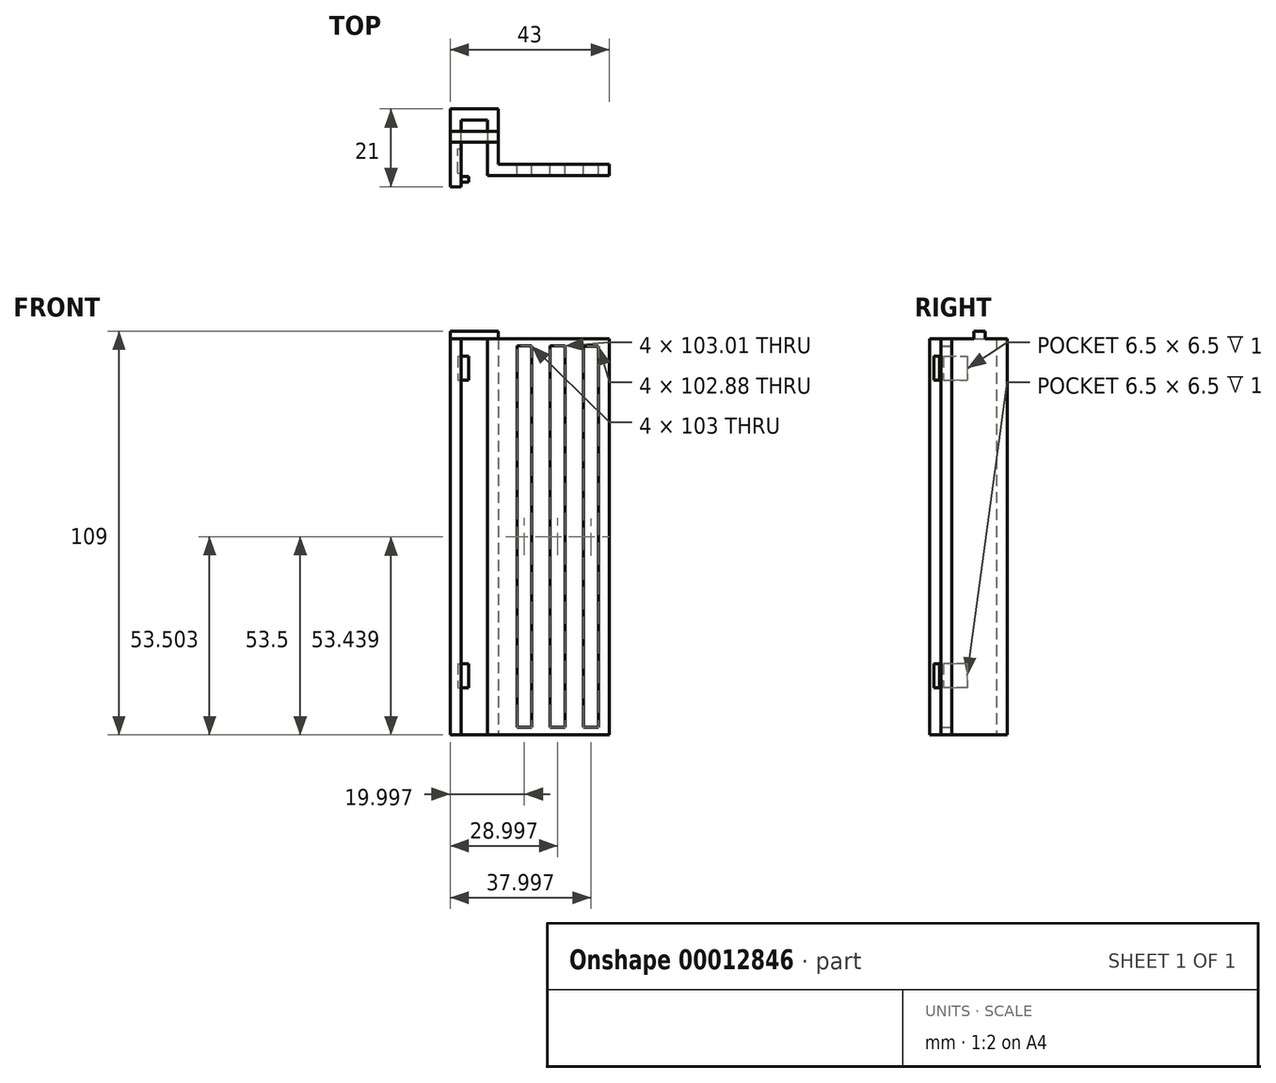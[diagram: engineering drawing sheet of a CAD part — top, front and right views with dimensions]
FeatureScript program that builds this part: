
annotation { "Feature Type Name" : "Feature", "Feature Type Description" : "" }
export const myFeature = defineFeature(function(context is Context, id is Id, definition is map)
    precondition{}
    {
        {
            var Q0;
            Q0=qCreatedBy(makeId("Top.planeOp"),FACE);
            var sketch = newSketch(context, id + "F0", { "sketchPlane" : qUnion([Q0])});
            skLineSegment(sketch, "E0", {"start": v(-54.2, 35.8) * mm, "end": v(-54.2, 56.8) * mm});
            skLineSegment(sketch, "E1", {"start": v(-54.2, 56.8) * mm, "end": v(-41.2, 56.8) * mm});
            skLineSegment(sketch, "E2", {"start": v(-41.2, 56.8) * mm, "end": v(-41.2, 41.8) * mm});
            skLineSegment(sketch, "E3", {"start": v(-41.2, 41.8) * mm, "end": v(-11.2, 41.8) * mm});
            skLineSegment(sketch, "E4", {"start": v(-54.2, 35.8) * mm, "end": v(-51.2, 35.8) * mm});
            skLineSegment(sketch, "E5", {"start": v(-51.2, 35.8) * mm, "end": v(-51.2, 53.8) * mm});
            skLineSegment(sketch, "E6", {"start": v(-51.2, 53.8) * mm, "end": v(-44.2, 53.8) * mm});
            skLineSegment(sketch, "E7", {"start": v(-44.2, 53.8) * mm, "end": v(-44.2, 38.8) * mm});
            skLineSegment(sketch, "E8", {"start": v(-44.2, 38.8) * mm, "end": v(-11.2, 38.8) * mm});
            skLineSegment(sketch, "E9", {"start": v(-11.2, 38.8) * mm, "end": v(-11.2, 41.8) * mm});
            skSolve(sketch);
        }
        {
            var Q0;
            Q0=makeQuery(id+"F0.imprint","IMPRINT",FACE,{"disambiguationData":[TD([[makeQuery(id+"F0.imprint","IMPRINT",EDGE,{"derivedFrom":sQuery(id+"F0.wireOp",EDGE,"E0")}),-1.0]])]});
            extrude(context, id + "F1", {"entities" : qUnion([Q0]), "depth" : 107 * mm});
        }
        {
            var Q0;
            Q0=makeQuery(id+"F1.opExtrude","SWEPT_FACE",FACE,{"disambiguationData":[OSD([sQuery(id+"F0.wireOp",EDGE,"E5")])]});
            var sketch = newSketch(context, id + "F2", { "sketchPlane" : qUnion([Q0])});
            skLineSegment(sketch, "E10.bottom", {"start": v(46, 19.2) * mm, "end": v(39.5, 19.2) * mm});
            skLineSegment(sketch, "E10.top", {"start": v(46, 12.7) * mm, "end": v(39.5, 12.7) * mm});
            skLineSegment(sketch, "E10.left", {"start": v(46, 19.2) * mm, "end": v(46, 12.7) * mm});
            skLineSegment(sketch, "E10.right", {"start": v(39.5, 19.2) * mm, "end": v(39.5, 12.7) * mm});
            skLineSegment(sketch, "E11.bottom", {"start": v(39.5, 102.2) * mm, "end": v(46, 102.2) * mm});
            skLineSegment(sketch, "E11.top", {"start": v(39.5, 95.7) * mm, "end": v(46, 95.7) * mm});
            skLineSegment(sketch, "E11.left", {"start": v(39.5, 102.2) * mm, "end": v(39.5, 95.7) * mm});
            skLineSegment(sketch, "E11.right", {"start": v(46, 102.2) * mm, "end": v(46, 95.7) * mm});
            skSolve(sketch);
        }
        {
            var Q0;
            Q0=qSketchRegion(id+"F2",true);
            extrude(context, id + "F3", {"entities" : qUnion([Q0]), "operationType" : NewBodyOperationType.REMOVE, "oppositeDirection" : true, "depth" : 1 * mm});
        }
        {
            var Q0;
            Q0=makeQuery(id+"F1.opExtrude","SWEPT_FACE",FACE,{"disambiguationData":[OSD([sQuery(id+"F0.wireOp",EDGE,"E5")])]});
            var sketch = newSketch(context, id + "F4", { "sketchPlane" : qUnion([Q0])});
            skLineSegment(sketch, "E12.bottom", {"start": v(38.5, 102.2) * mm, "end": v(37, 102.2) * mm});
            skLineSegment(sketch, "E12.top", {"start": v(38.5, 95.7) * mm, "end": v(37, 95.7) * mm});
            skLineSegment(sketch, "E12.left", {"start": v(38.5, 102.2) * mm, "end": v(38.5, 95.7) * mm});
            skLineSegment(sketch, "E12.right", {"start": v(37, 102.2) * mm, "end": v(37, 95.7) * mm});
            skLineSegment(sketch, "E13.bottom", {"start": v(38.5, 19.2) * mm, "end": v(37, 19.2) * mm});
            skLineSegment(sketch, "E13.top", {"start": v(38.5, 12.7) * mm, "end": v(37, 12.7) * mm});
            skLineSegment(sketch, "E13.left", {"start": v(38.5, 19.2) * mm, "end": v(38.5, 12.7) * mm});
            skLineSegment(sketch, "E13.right", {"start": v(37, 19.2) * mm, "end": v(37, 12.7) * mm});
            skSolve(sketch);
        }
        {
            var Q0;
            Q0 = qSketchRegion(id + "F4", true);
            extrude(context, id + "F5", {"entities" : qUnion([Q0]), "operationType" : NewBodyOperationType.ADD, "depth" : 2 * mm});
        }
        {
            var Q0;
            Q0=makeQuery(id+"F1.opExtrude","SWEPT_FACE",FACE,{"disambiguationData":[OSD([sQuery(id+"F0.wireOp",EDGE,"E3")])]});
            var sketch = newSketch(context, id + "F6", { "sketchPlane" : qUnion([Q0])});
            skLineSegment(sketch, "E14.bottom", {"start": v(32.2, 105) * mm, "end": v(36.2, 105) * mm});
            skLineSegment(sketch, "E14.top", {"start": v(32.2, 2) * mm, "end": v(36.2, 2) * mm});
            skLineSegment(sketch, "E14.left", {"start": v(32.2, 105) * mm, "end": v(32.2, 2) * mm});
            skLineSegment(sketch, "E14.right", {"start": v(36.2, 105) * mm, "end": v(36.2, 2) * mm});
            skLineSegment(sketch, "E15.bottom", {"start": v(27.2, 105) * mm, "end": v(23.2, 105) * mm});
            skLineSegment(sketch, "E15.top", {"start": v(27.2, 2) * mm, "end": v(23.2, 2) * mm});
            skLineSegment(sketch, "E15.left", {"start": v(27.2, 105) * mm, "end": v(27.2, 2) * mm});
            skLineSegment(sketch, "E15.right", {"start": v(23.2, 105) * mm, "end": v(23.2, 2) * mm});
            skLineSegment(sketch, "E16.bottom", {"start": v(18.2, 104.88) * mm, "end": v(14.2, 104.88) * mm});
            skLineSegment(sketch, "E16.top", {"start": v(18.2, 2) * mm, "end": v(14.2, 2) * mm});
            skLineSegment(sketch, "E16.left", {"start": v(18.2, 104.88) * mm, "end": v(18.2, 2) * mm});
            skLineSegment(sketch, "E16.right", {"start": v(14.2, 104.88) * mm, "end": v(14.2, 2) * mm});
            skSolve(sketch);
        }
        {
            var Q0;
            Q0 = qSketchRegion(id + "F6", true);
            extrude(context, id + "F7", {"entities" : qUnion([Q0]), "operationType" : NewBodyOperationType.REMOVE, "oppositeDirection" : true, "depth" : 3 * mm});
        }
        {
            var Q0;
            Q0=makeQuery(id+"F1.opExtrude","CAP_FACE",FACE,{"disambiguationData":[OSD([sQuery(id+"F0.wireOp",EDGE,"E0"),sQuery(id+"F0.wireOp",EDGE,"E1"),sQuery(id+"F0.wireOp",EDGE,"E2"),sQuery(id+"F0.wireOp",EDGE,"E3"),sQuery(id+"F0.wireOp",EDGE,"E4"),sQuery(id+"F0.wireOp",EDGE,"E5"),sQuery(id+"F0.wireOp",EDGE,"E6"),sQuery(id+"F0.wireOp",EDGE,"E7"),sQuery(id+"F0.wireOp",EDGE,"E8"),sQuery(id+"F0.wireOp",EDGE,"E9")])],"isStart":false});
            var sketch = newSketch(context, id + "F8", { "sketchPlane" : qUnion([Q0])});
            skLineSegment(sketch, "E17.bottom", {"start": v(-54.2, 50.8) * mm, "end": v(-41.2, 50.8) * mm});
            skLineSegment(sketch, "E17.top", {"start": v(-54.2, 47.8) * mm, "end": v(-41.2, 47.8) * mm});
            skLineSegment(sketch, "E17.left", {"start": v(-54.2, 50.8) * mm, "end": v(-54.2, 47.8) * mm});
            skLineSegment(sketch, "E17.right", {"start": v(-41.2, 50.8) * mm, "end": v(-41.2, 47.8) * mm});
            skSolve(sketch);
        }
        {
            var Q0;
            Q0 = qSketchRegion(id + "F8", true);
            extrude(context, id + "F9", {"entities" : qUnion([Q0]), "operationType" : NewBodyOperationType.ADD, "depth" : 2 * mm});
        }
    });
